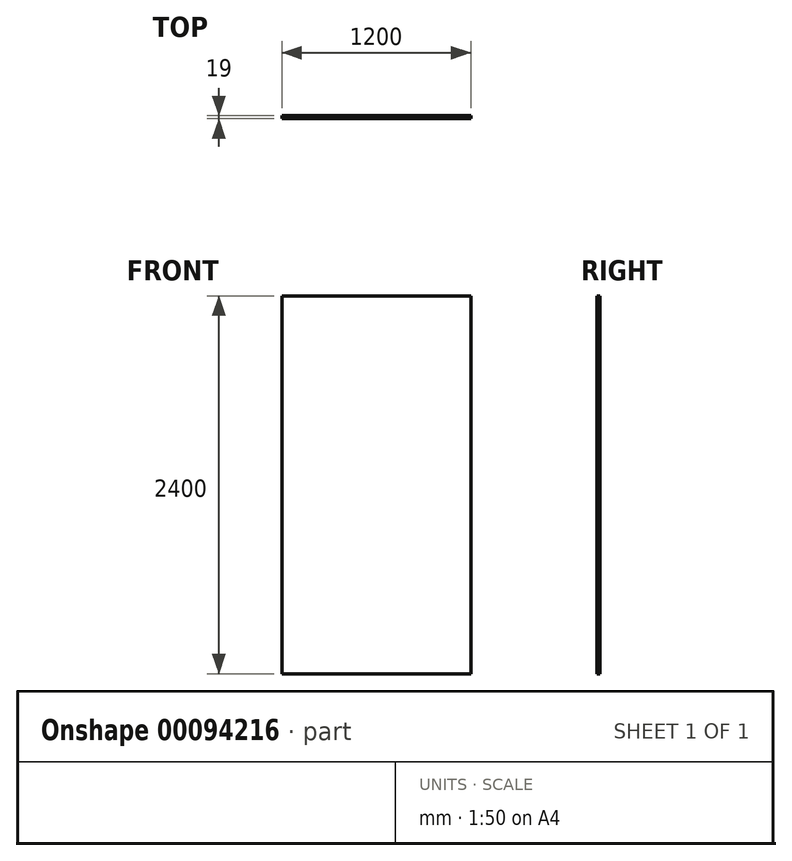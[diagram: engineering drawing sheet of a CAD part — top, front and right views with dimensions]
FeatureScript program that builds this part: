
annotation { "Feature Type Name" : "Feature", "Feature Type Description" : "" }
export const myFeature = defineFeature(function(context is Context, id is Id, definition is map)
    precondition{}
    {
        {
            var Q0;
            Q0=qCreatedBy(makeId("Front.planeOp"),FACE);
            var sketch = newSketch(context, id + "F0", { "sketchPlane" : qUnion([Q0])});
            skLineSegment(sketch, "E0.bottom", {"start": v(600, -1200) * mm, "end": v(-600, -1200) * mm});
            skLineSegment(sketch, "E0.top", {"start": v(600, 1200) * mm, "end": v(-600, 1200) * mm});
            skLineSegment(sketch, "E0.left", {"start": v(600, -1200) * mm, "end": v(600, 1200) * mm});
            skLineSegment(sketch, "E0.right", {"start": v(-600, -1200) * mm, "end": v(-600, 1200) * mm});
            skPoint(sketch, "E0.middle", {"position": v(0, 0) * mm});
            skLineSegment(sketch, "E1", {"start": v(0, -1200) * mm, "end": v(0, 1200) * mm});
            skSolve(sketch);
        }
        {
            var Q0;
            Q0=makeQuery(id+"F0.imprint","IMPRINT",FACE,{"disambiguationData":[TD([[makeQuery(id+"F0.imprint","IMPRINT",EDGE,{"derivedFrom":sQuery(id+"F0.wireOp",EDGE,"E0.bottom")}),-1.0]])]});
            extrude(context, id + "F1", {"entities" : qUnion([Q0]), "endBound" : BoundingType.SYMMETRIC, "depth" : 19 * mm});
        }
    });
